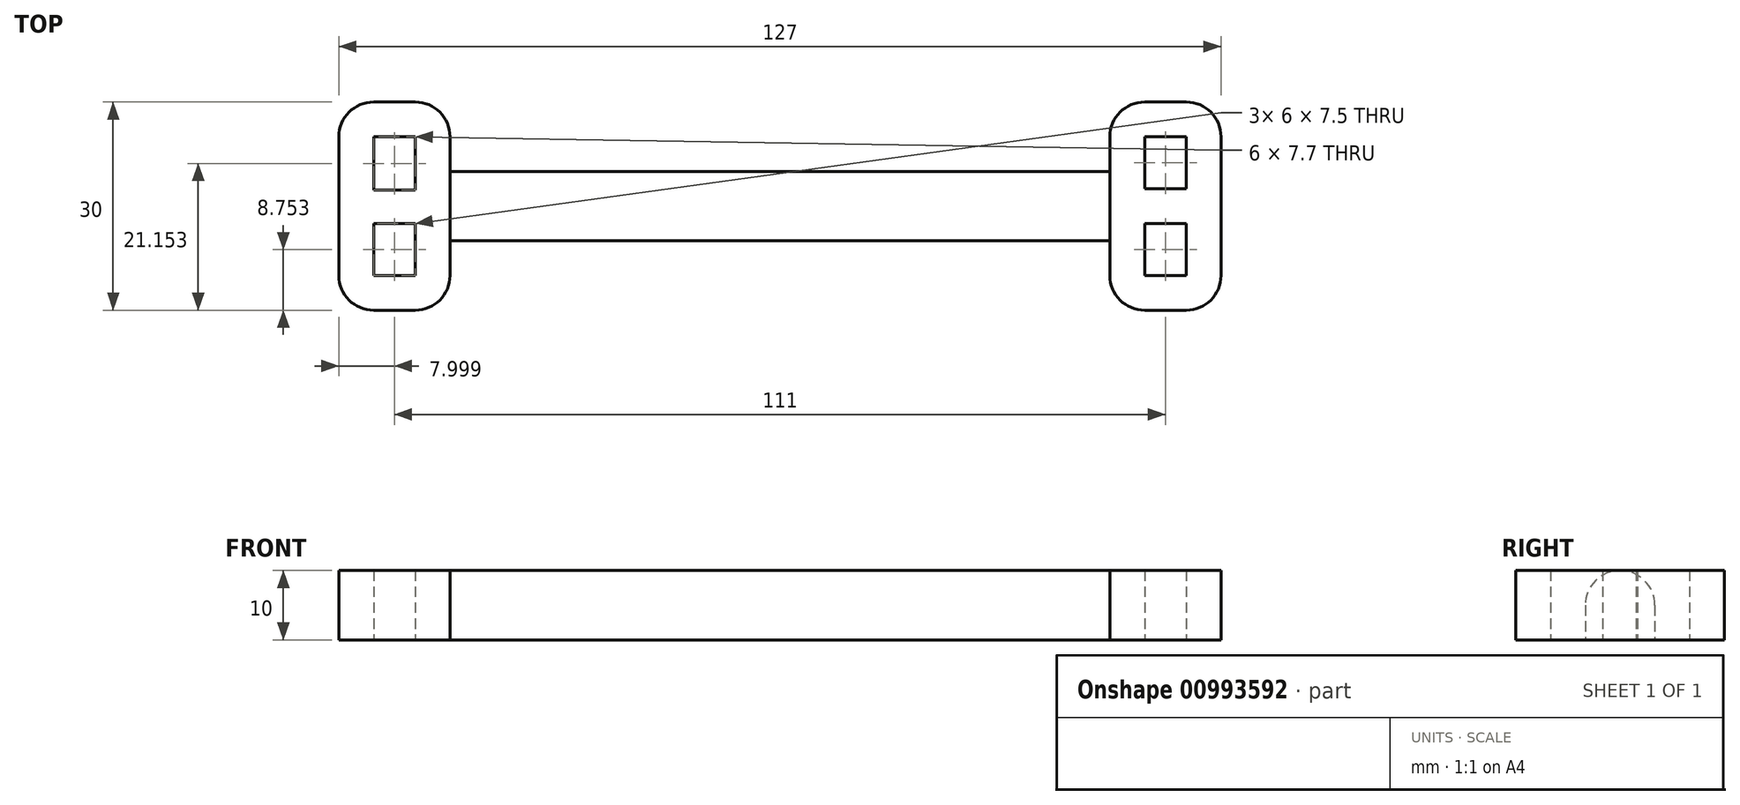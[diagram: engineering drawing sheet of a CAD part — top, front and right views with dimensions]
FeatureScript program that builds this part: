
annotation { "Feature Type Name" : "Feature", "Feature Type Description" : "" }
export const myFeature = defineFeature(function(context is Context, id is Id, definition is map)
    precondition{}
    {
        {
            var Q0;
            Q0=qCreatedBy(makeId("Top.planeOp"),FACE);
            var sketch = newSketch(context, id + "F0", { "sketchPlane" : qUnion([Q0])});
            skLineSegment(sketch, "E0.bottom", {"start": v(-46.56, 30.46) * mm, "end": v(48.44, 30.46) * mm});
            skLineSegment(sketch, "E0.top", {"start": v(-46.56, 20.46) * mm, "end": v(48.44, 20.46) * mm});
            skLineSegment(sketch, "E0.left", {"start": v(-46.56, 30.46) * mm, "end": v(-46.56, 20.46) * mm});
            skLineSegment(sketch, "E0.right", {"start": v(48.44, 30.46) * mm, "end": v(48.44, 20.46) * mm});
            skLineSegment(sketch, "E1.bottom", {"start": v(48.44, 10.46) * mm, "end": v(64.44, 10.46) * mm});
            skLineSegment(sketch, "E1.top", {"start": v(48.44, 40.46) * mm, "end": v(64.44, 40.46) * mm});
            skLineSegment(sketch, "E1.left", {"start": v(48.44, 10.46) * mm, "end": v(48.44, 40.46) * mm});
            skLineSegment(sketch, "E1.right", {"start": v(64.44, 10.46) * mm, "end": v(64.44, 40.46) * mm});
            skPoint(sketch, "E2.firstSnap0", {"position": v(-46.56, 25.46) * mm});
            skLineSegment(sketch, "E2.bottom", {"start": v(-46.56, 10.46) * mm, "end": v(-62.56, 10.46) * mm});
            skLineSegment(sketch, "E2.top", {"start": v(-46.56, 40.46) * mm, "end": v(-62.56, 40.46) * mm});
            skLineSegment(sketch, "E2.left", {"start": v(-46.56, 10.46) * mm, "end": v(-46.56, 40.46) * mm});
            skLineSegment(sketch, "E2.right", {"start": v(-62.56, 10.46) * mm, "end": v(-62.56, 40.46) * mm});
            skLineSegment(sketch, "E3.bottom", {"start": v(-57.56, 35.46) * mm, "end": v(-51.56, 35.46) * mm});
            skLineSegment(sketch, "E3.top", {"start": v(-57.56, 27.76) * mm, "end": v(-51.56, 27.76) * mm});
            skLineSegment(sketch, "E3.left", {"start": v(-57.56, 35.46) * mm, "end": v(-57.56, 27.76) * mm});
            skLineSegment(sketch, "E3.right", {"start": v(-51.56, 35.46) * mm, "end": v(-51.56, 27.76) * mm});
            skLineSegment(sketch, "E4.bottom", {"start": v(-57.56, 22.96) * mm, "end": v(-51.56, 22.96) * mm});
            skLineSegment(sketch, "E4.top", {"start": v(-57.56, 15.46) * mm, "end": v(-51.56, 15.46) * mm});
            skLineSegment(sketch, "E4.left", {"start": v(-57.56, 22.96) * mm, "end": v(-57.56, 15.46) * mm});
            skLineSegment(sketch, "E4.right", {"start": v(-51.56, 22.96) * mm, "end": v(-51.56, 15.46) * mm});
            skLineSegment(sketch, "E5.bottom", {"start": v(53.44, 35.46) * mm, "end": v(59.44, 35.46) * mm});
            skLineSegment(sketch, "E5.top", {"start": v(53.44, 27.96) * mm, "end": v(59.44, 27.96) * mm});
            skLineSegment(sketch, "E5.left", {"start": v(53.44, 35.46) * mm, "end": v(53.44, 27.96) * mm});
            skLineSegment(sketch, "E5.right", {"start": v(59.44, 35.46) * mm, "end": v(59.44, 27.96) * mm});
            skLineSegment(sketch, "E6.bottom", {"start": v(53.44, 22.96) * mm, "end": v(59.44, 22.96) * mm});
            skLineSegment(sketch, "E6.top", {"start": v(53.44, 15.46) * mm, "end": v(59.44, 15.46) * mm});
            skLineSegment(sketch, "E6.left", {"start": v(53.44, 22.96) * mm, "end": v(53.44, 15.46) * mm});
            skLineSegment(sketch, "E6.right", {"start": v(59.44, 22.96) * mm, "end": v(59.44, 15.46) * mm});
            skSolve(sketch);
        }
        {
            var Q0;
            {var subQ3=sQuery(id+"F0.wireOp",EDGE,"E2.bottom");Q0=makeQuery(id+"F0.imprint","IMPRINT",FACE,{"disambiguationData":[TD([[makeQuery(id+"F0.imprint","IMPRINT",EDGE,{"derivedFrom":subQ3}),-1.0]])]});}
            var Q1;
            {var subQ3=sQuery(id+"F0.wireOp",EDGE,"E1.bottom");Q1=makeQuery(id+"F0.imprint","IMPRINT",FACE,{"disambiguationData":[TD([[makeQuery(id+"F0.imprint","IMPRINT",EDGE,{"derivedFrom":subQ3}),1.0]])]});}
            extrude(context, id + "F1", {"entities" : qUnion([Q0, Q1]), "depth" : 10 * mm, "offsetDistance" : 25 * mm});
        }
        {
            var Q0;
            {var subQ0=sQuery(id+"F0.wireOp",EDGE,"E0.bottom");Q0=makeQuery(id+"F0.imprint","IMPRINT",FACE,{"disambiguationData":[TD([[makeQuery(id+"F0.imprint","IMPRINT",EDGE,{"derivedFrom":subQ0}),-1.0]])]});}
            extrude(context, id + "F2", {"entities" : qUnion([Q0]), "depth" : 10 * mm, "offsetDistance" : 25 * mm});
        }
        {
            var Q0;
            Q0=makeQuery(id+"F2.opExtrude","CAP_EDGE",EDGE,{"disambiguationData":[OSD([sQuery(id+"F0.wireOp",EDGE,"E0.top")])],"isStart":false});
            var Q1;
            Q1=makeQuery(id+"F2.opExtrude","CAP_EDGE",EDGE,{"disambiguationData":[OSD([sQuery(id+"F0.wireOp",EDGE,"E0.bottom")])],"isStart":false});
            fillet(context, id + "F3", {"entities" : qUnion([Q0, Q1]), "radius" : 5 * mm, "tangentPropagation" : true, "allowEdgeOverflow" : false});
        }
        {
            var Q0;
            Q0=makeQuery(id+"F1.opExtrude","SWEPT_EDGE",EDGE,{"disambiguationData":[OSD([sQuery(id+"F0.wireOp",EDGE,"E2.bottom"),sQuery(id+"F0.wireOp",EDGE,"E2.right")])]});
            var Q1;
            Q1=makeQuery(id+"F1.opExtrude","SWEPT_EDGE",EDGE,{"disambiguationData":[OSD([sQuery(id+"F0.wireOp",EDGE,"E2.bottom"),sQuery(id+"F0.wireOp",EDGE,"E2.left")])]});
            var Q2;
            Q2=makeQuery(id+"F1.opExtrude","SWEPT_EDGE",EDGE,{"disambiguationData":[OSD([sQuery(id+"F0.wireOp",EDGE,"E1.bottom"),sQuery(id+"F0.wireOp",EDGE,"E1.left")])]});
            var Q3;
            Q3=makeQuery(id+"F1.opExtrude","SWEPT_EDGE",EDGE,{"disambiguationData":[OSD([sQuery(id+"F0.wireOp",EDGE,"E1.bottom"),sQuery(id+"F0.wireOp",EDGE,"E1.right")])]});
            var Q4;
            Q4=makeQuery(id+"F1.opExtrude","SWEPT_EDGE",EDGE,{"disambiguationData":[OSD([sQuery(id+"F0.wireOp",EDGE,"E1.top"),sQuery(id+"F0.wireOp",EDGE,"E1.right")])]});
            var Q5;
            Q5=makeQuery(id+"F1.opExtrude","SWEPT_EDGE",EDGE,{"disambiguationData":[OSD([sQuery(id+"F0.wireOp",EDGE,"E1.top"),sQuery(id+"F0.wireOp",EDGE,"E1.left")])]});
            var Q6;
            Q6=makeQuery(id+"F1.opExtrude","SWEPT_EDGE",EDGE,{"disambiguationData":[OSD([sQuery(id+"F0.wireOp",EDGE,"E2.top"),sQuery(id+"F0.wireOp",EDGE,"E2.left")])]});
            var Q7;
            Q7=makeQuery(id+"F1.opExtrude","SWEPT_EDGE",EDGE,{"disambiguationData":[OSD([sQuery(id+"F0.wireOp",EDGE,"E2.top"),sQuery(id+"F0.wireOp",EDGE,"E2.right")])]});
            fillet(context, id + "F4", {"entities" : qUnion([Q0, Q1, Q2, Q3, Q4, Q5, Q6, Q7]), "radius" : 5 * mm, "tangentPropagation" : true, "allowEdgeOverflow" : false});
        }
    });
